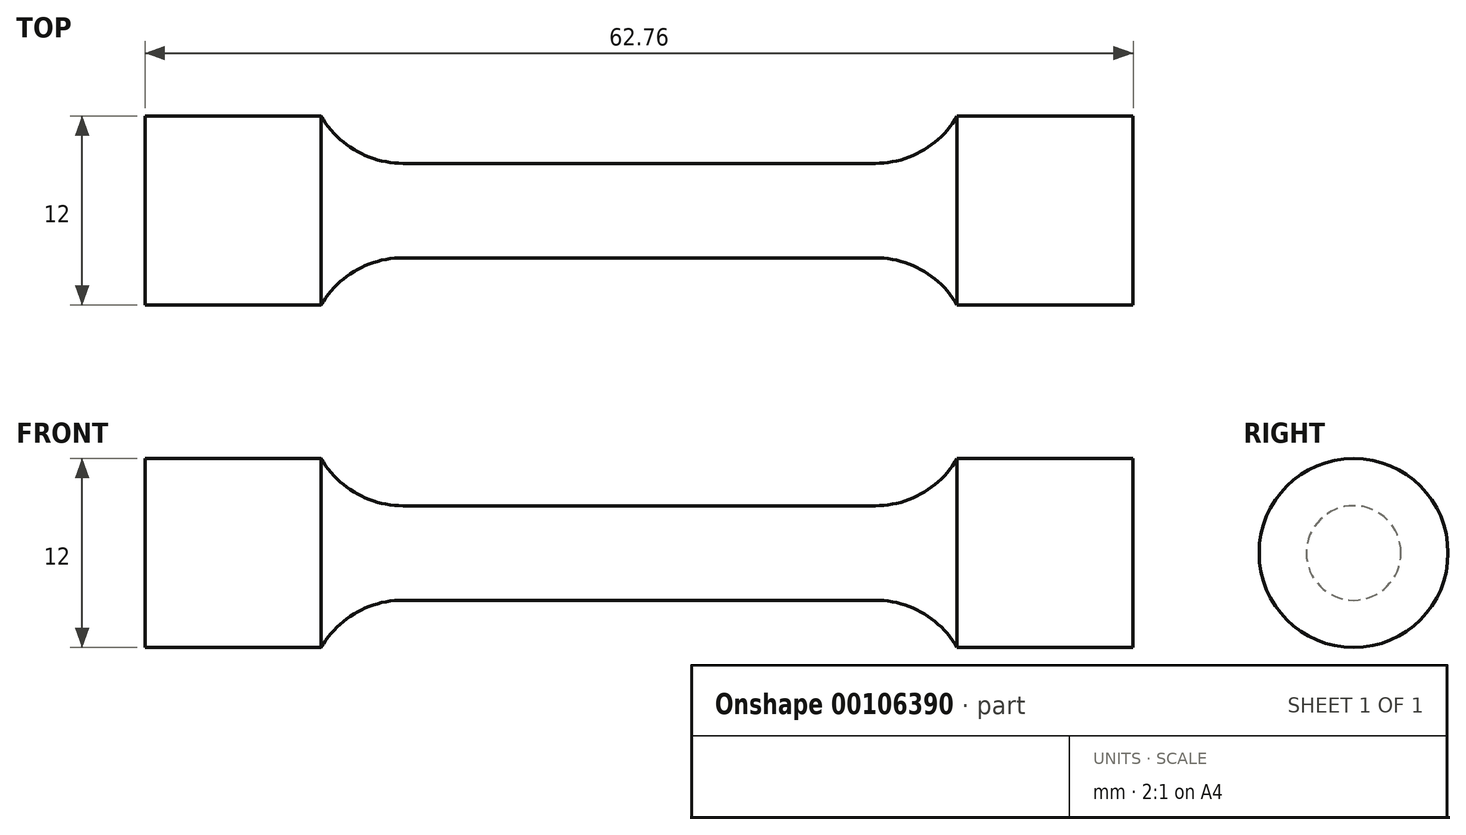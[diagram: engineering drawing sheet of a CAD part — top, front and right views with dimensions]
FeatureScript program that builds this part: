
annotation { "Feature Type Name" : "Feature", "Feature Type Description" : "" }
export const myFeature = defineFeature(function(context is Context, id is Id, definition is map)
    precondition{}
    {
        {
            var Q0;
            Q0=qCreatedBy(makeId("Front.planeOp"),FACE);
            var sketch = newSketch(context, id + "F0", { "sketchPlane" : qUnion([Q0])});
            skLineSegment(sketch, "E0", {"start": v(-33.4, 0) * mm, "end": v(40.08, 0) * mm, "construction": true});
            skLineSegment(sketch, "E1", {"start": v(0, 28.1) * mm, "end": v(0, -22.78) * mm, "construction": true});
            skLineSegment(sketch, "E2", {"start": v(-15, 3) * mm, "end": v(15, 3) * mm});
            skLineSegment(sketch, "E3", {"start": v(-31.38, 6) * mm, "end": v(-20.2, 6) * mm});
            skPoint(sketch, "E4", {"position": v(0, 6) * mm});
            skPoint(sketch, "E5", {"position": v(0, 3) * mm});
            skArc(sketch, "E6", {"start": v(15, 3) * mm, "mid": v(18, 3.8) * mm, "end": v(20.2, 6) * mm});
            skLineSegment(sketch, "E7", {"start": v(31.38, 6) * mm, "end": v(31.38, 0) * mm});
            skLineSegment(sketch, "E8.MirrorCS", {"start": v(-31.38, 6) * mm, "end": v(-31.38, 0) * mm});
            skArc(sketch, "E9.MirrorCS", {"start": v(-15, 3) * mm, "mid": v(-18, 3.8) * mm, "end": v(-20.2, 6) * mm});
            skLineSegment(sketch, "E10", {"start": v(-31.38, 0) * mm, "end": v(31.38, 0) * mm});
            skLineSegment(sketch, "E11.trimOffspring", {"start": v(20.2, 6) * mm, "end": v(31.38, 6) * mm});
            skSolve(sketch);
        }
        {
            var Q0;
            Q0 = qSketchRegion(id + "F0", true);
            var Q1;
            Q1=sQuery(id+"F0.wireOp",EDGE,"E10");
            revolve(context, id + "F1", {"entities" : qUnion([Q0]), "axis" : qUnion([Q1]), "revolveType" : RevolveType.FULL});
        }
    });
